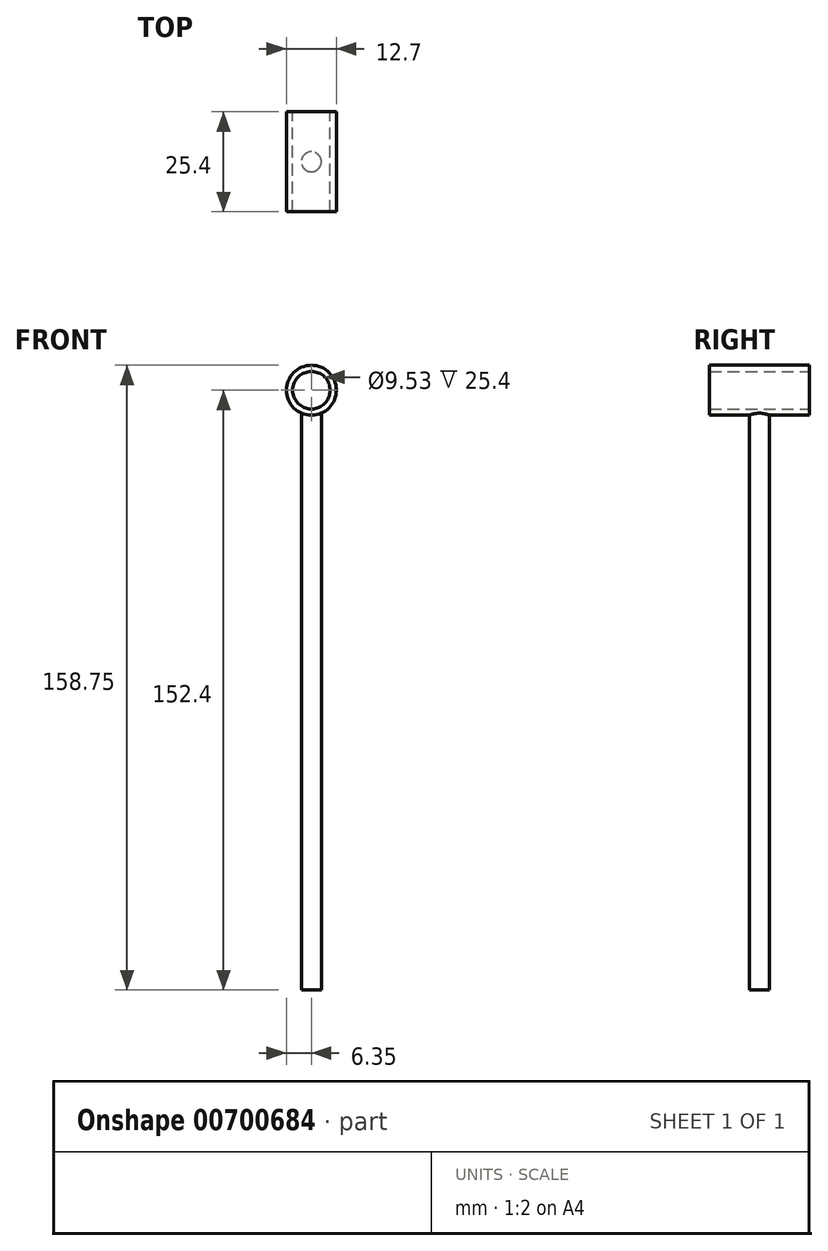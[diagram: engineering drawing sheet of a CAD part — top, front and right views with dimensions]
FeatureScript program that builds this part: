
annotation { "Feature Type Name" : "Feature", "Feature Type Description" : "" }
export const myFeature = defineFeature(function(context is Context, id is Id, definition is map)
    precondition{}
    {
        {
            var Q0;
            Q0=qCreatedBy(makeId("Front.planeOp"),FACE);
            var sketch = newSketch(context, id + "F0", { "sketchPlane" : qUnion([Q0])});
            skCircle(sketch, "E0", {"center": v(0, 0) * mm, "radius": 4.76 * mm});
            skCircle(sketch, "E1", {"center": v(0, 0) * mm, "radius": 6.35 * mm});
            skSolve(sketch);
        }
        {
            var Q0;
            Q0 = qSketchRegion(id + "F0", true);
            extrude(context, id + "F1", {"entities" : qUnion([Q0]), "depth" : 25.4 * mm, "offsetDistance" : 25.4 * mm});
        }
        {
            var Q0;
            Q0=qCreatedBy(makeId("Top.planeOp"),FACE);
            var sketch = newSketch(context, id + "F2", { "sketchPlane" : qUnion([Q0])});
            skPoint(sketch, "E2", {"position": v(0, -12.7) * mm});
            skPoint(sketch, "E3", {"position": v(-32.14, 3.94) * mm});
            skLineSegment(sketch, "E4.0", {"start": v(6.35, -25.4) * mm, "end": v(-6.35, -25.4) * mm});
            skPoint(sketch, "E5", {"position": v(0, -25.4) * mm});
            skLineSegment(sketch, "E6", {"start": v(6.35, 0) * mm, "end": v(6.35, -25.4) * mm});
            skLineSegment(sketch, "E7", {"start": v(-6.35, -25.4) * mm, "end": v(-6.35, 0) * mm});
            skPoint(sketch, "E8", {"position": v(0, 0) * mm});
            skCircle(sketch, "E9", {"center": v(0, -12.7) * mm, "radius": 2.54 * mm});
            skSolve(sketch);
        }
        {
            var Q0;
            Q0 = qSketchRegion(id + "F2", true);
            extrude(context, id + "F3", {"entities" : qUnion([Q0]), "operationType" : NewBodyOperationType.ADD, "oppositeDirection" : true, "depth" : 152.4 * mm, "offsetDistance" : 25.4 * mm});
        }
        {
            var Q0;
            Q0=makeQuery(id+"F1.opExtrude","CAP_FACE",FACE,{"disambiguationData":[OSD([sQuery(id+"F0.wireOp",EDGE,"E0"),sQuery(id+"F0.wireOp",EDGE,"E1")])],"isStart":false});
            var sketch = newSketch(context, id + "F4", { "sketchPlane" : qUnion([Q0])});
            skCircle(sketch, "E10.0", {"center": v(0, 0) * mm, "radius": 4.76 * mm});
            skSolve(sketch);
        }
        {
            var Q0;
            Q0 = qSketchRegion(id + "F4", true);
            extrude(context, id + "F5", {"entities" : qUnion([Q0]), "operationType" : NewBodyOperationType.REMOVE, "oppositeDirection" : true, "depth" : 25.4 * mm, "offsetDistance" : 25.4 * mm});
        }
    });
